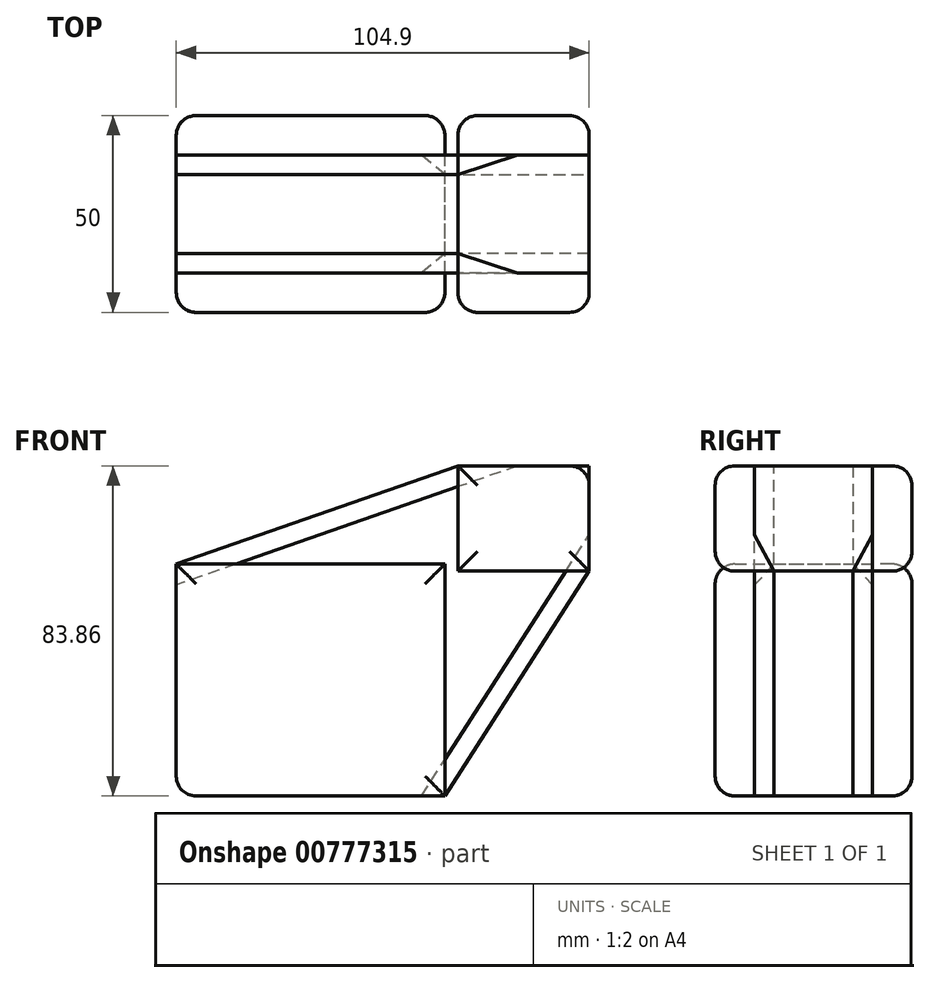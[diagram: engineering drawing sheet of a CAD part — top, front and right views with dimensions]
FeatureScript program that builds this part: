
annotation { "Feature Type Name" : "Feature", "Feature Type Description" : "" }
export const myFeature = defineFeature(function(context is Context, id is Id, definition is map)
    precondition{}
    {
        {
            var Q0;
            Q0=qCreatedBy(makeId("Front.planeOp"),FACE);
            var sketch = newSketch(context, id + "F0", { "sketchPlane" : qUnion([Q0])});
            skLineSegment(sketch, "E0.bottom", {"start": v(-34.72, 27.2) * mm, "end": v(33.51, 27.2) * mm});
            skLineSegment(sketch, "E0.top", {"start": v(-34.72, -31.71) * mm, "end": v(33.51, -31.71) * mm});
            skLineSegment(sketch, "E0.left", {"start": v(-34.72, 27.2) * mm, "end": v(-34.72, -31.71) * mm});
            skLineSegment(sketch, "E0.right", {"start": v(33.51, 27.2) * mm, "end": v(33.51, -31.71) * mm});
            skLineSegment(sketch, "E1.bottom", {"start": v(36.82, 52.15) * mm, "end": v(70.18, 52.15) * mm});
            skLineSegment(sketch, "E1.top", {"start": v(36.82, 25.4) * mm, "end": v(70.18, 25.4) * mm});
            skLineSegment(sketch, "E1.left", {"start": v(36.82, 52.15) * mm, "end": v(36.82, 25.4) * mm});
            skLineSegment(sketch, "E1.right", {"start": v(70.18, 52.15) * mm, "end": v(70.18, 25.4) * mm});
            skLineSegment(sketch, "E2", {"start": v(-34.72, 27.2) * mm, "end": v(36.82, 52.15) * mm});
            skLineSegment(sketch, "E3", {"start": v(33.51, -31.71) * mm, "end": v(70.18, 25.4) * mm});
            skSolve(sketch);
        }
        {
            var Q0;
            Q0=makeQuery(id+"F0.imprint","IMPRINT",FACE,{"disambiguationData":[TD([[makeQuery(id+"F0.imprint","IMPRINT",EDGE,{"derivedFrom":sQuery(id+"F0.wireOp",EDGE,"E0.bottom")}),-1.0]])]});
            var Q1;
            Q1=makeQuery(id+"F0.imprint","IMPRINT",FACE,{"disambiguationData":[TD([[makeQuery(id+"F0.imprint","IMPRINT",EDGE,{"derivedFrom":sQuery(id+"F0.wireOp",EDGE,"E1.bottom")}),-1.0]])]});
            extrude(context, id + "F1", {"entities" : qUnion([Q0, Q1]), "depth" : 40 * mm, "offsetDistance" : 25 * mm});
        }
        {
            var Q0;
            Q0 = qSketchRegion(id + "F0", true);
            extrude(context, id + "F2", {"entities" : qUnion([Q0]), "depth" : 30 * mm, "offsetDistance" : 25 * mm});
        }
        {
            var Q0;
            Q0=makeQuery(id+"F1.opExtrude","CAP_EDGE",EDGE,{"disambiguationData":[OSD([sQuery(id+"F0.wireOp",EDGE,"E0.bottom")])],"isStart":false});
            var Q1;
            Q1=makeQuery(id+"F1.opExtrude","CAP_EDGE",EDGE,{"disambiguationData":[OSD([sQuery(id+"F0.wireOp",EDGE,"E0.left")])],"isStart":false});
            var Q2;
            Q2=makeQuery(id+"F1.opExtrude","CAP_EDGE",EDGE,{"disambiguationData":[OSD([sQuery(id+"F0.wireOp",EDGE,"E0.top")])],"isStart":false});
            var Q3;
            Q3=makeQuery(id+"F1.opExtrude","CAP_EDGE",EDGE,{"disambiguationData":[OSD([sQuery(id+"F0.wireOp",EDGE,"E0.right")])],"isStart":false});
            fillet(context, id + "F3", {"entities" : qUnion([Q0, Q1, Q2, Q3]), "radius" : 5 * mm, "tangentPropagation" : true, "allowEdgeOverflow" : false});
        }
        {
            var Q0;
            Q0=makeQuery(id+"F2.opExtrude","CAP_EDGE",EDGE,{"disambiguationData":[OSD([sQuery(id+"F0.wireOp",EDGE,"E2")])],"isStart":false});
            var Q1;
            Q1=makeQuery(id+"F2.opExtrude","CAP_EDGE",EDGE,{"disambiguationData":[OSD([sQuery(id+"F0.wireOp",EDGE,"E2")])],"isStart":true});
            var Q2;
            Q2=makeQuery(id+"F2.opExtrude","CAP_EDGE",EDGE,{"disambiguationData":[OSD([sQuery(id+"F0.wireOp",EDGE,"E3")])],"isStart":false});
            var Q3;
            Q3=makeQuery(id+"F2.opExtrude","CAP_EDGE",EDGE,{"disambiguationData":[OSD([sQuery(id+"F0.wireOp",EDGE,"E3")])],"isStart":true});
            chamfer(context, id + "F4", {"entities" : qUnion([Q0, Q1, Q2, Q3]), "width" : 5 * mm, "tangentPropagation" : true});
        }
        {
            var Q0;
            Q0=makeQuery(id+"F1.opExtrude","CAP_FACE",FACE,{"disambiguationData":[OSD([sQuery(id+"F0.wireOp",EDGE,"E0.bottom"),sQuery(id+"F0.wireOp",EDGE,"E0.top"),sQuery(id+"F0.wireOp",EDGE,"E0.left"),sQuery(id+"F0.wireOp",EDGE,"E0.right")])],"isStart":true});
            var Q1;
            Q1=makeQuery(id+"F1.opExtrude","CAP_FACE",FACE,{"disambiguationData":[OSD([sQuery(id+"F0.wireOp",EDGE,"E1.bottom"),sQuery(id+"F0.wireOp",EDGE,"E1.top"),sQuery(id+"F0.wireOp",EDGE,"E1.left"),sQuery(id+"F0.wireOp",EDGE,"E1.right")])],"isStart":true});
            extrude(context, id + "F5", {"entities" : qUnion([Q0, Q1]), "depth" : 10 * mm, "offsetDistance" : 25 * mm});
        }
        {
            var Q0;
            Q0=makeQuery(id+"F1.opExtrude","CAP_EDGE",EDGE,{"disambiguationData":[OSD([sQuery(id+"F0.wireOp",EDGE,"E1.left")])],"isStart":false});
            var Q1;
            Q1=makeQuery(id+"F1.opExtrude","CAP_EDGE",EDGE,{"disambiguationData":[OSD([sQuery(id+"F0.wireOp",EDGE,"E1.right")])],"isStart":false});
            var Q2;
            Q2=makeQuery(id+"F1.opExtrude","CAP_EDGE",EDGE,{"disambiguationData":[OSD([sQuery(id+"F0.wireOp",EDGE,"E1.top")])],"isStart":false});
            var Q3;
            Q3=makeQuery(id+"F1.opExtrude","CAP_EDGE",EDGE,{"disambiguationData":[OSD([sQuery(id+"F0.wireOp",EDGE,"E1.bottom")])],"isStart":false});
            var Q4;
            Q4=makeQuery(id+"F5.opExtrude","CAP_EDGE",EDGE,{"disambiguationData":[OSD([sQuery(id+"F0.wireOp",EDGE,"E1.bottom")])],"isStart":false});
            var Q5;
            Q5=makeQuery(id+"F5.opExtrude","CAP_EDGE",EDGE,{"disambiguationData":[OSD([sQuery(id+"F0.wireOp",EDGE,"E1.right")])],"isStart":false});
            var Q6;
            Q6=makeQuery(id+"F5.opExtrude","CAP_EDGE",EDGE,{"disambiguationData":[OSD([sQuery(id+"F0.wireOp",EDGE,"E1.top")])],"isStart":false});
            var Q7;
            Q7=makeQuery(id+"F5.opExtrude","CAP_EDGE",EDGE,{"disambiguationData":[OSD([sQuery(id+"F0.wireOp",EDGE,"E1.left")])],"isStart":false});
            var Q8;
            Q8=makeQuery(id+"F5.opExtrude","CAP_EDGE",EDGE,{"disambiguationData":[OSD([sQuery(id+"F0.wireOp",EDGE,"E0.bottom")])],"isStart":false});
            var Q9;
            Q9=makeQuery(id+"F5.opExtrude","CAP_EDGE",EDGE,{"disambiguationData":[OSD([sQuery(id+"F0.wireOp",EDGE,"E0.right")])],"isStart":false});
            var Q10;
            Q10=makeQuery(id+"F5.opExtrude","CAP_EDGE",EDGE,{"disambiguationData":[OSD([sQuery(id+"F0.wireOp",EDGE,"E0.left")])],"isStart":false});
            var Q11;
            Q11=makeQuery(id+"F5.opExtrude","CAP_EDGE",EDGE,{"disambiguationData":[OSD([sQuery(id+"F0.wireOp",EDGE,"E0.top")])],"isStart":false});
            var Q12;
            Q12=makeQuery(id+"F1.opExtrude","SWEPT_EDGE",EDGE,{"disambiguationData":[OSD([sQuery(id+"F0.wireOp",EDGE,"E1.bottom"),sQuery(id+"F0.wireOp",EDGE,"E1.right")])]});
            var Q13;
            Q13=makeQuery(id+"F5.opExtrude","SWEPT_EDGE",EDGE,{"disambiguationData":[OSD([sQuery(id+"F0.wireOp",EDGE,"E1.bottom"),sQuery(id+"F0.wireOp",EDGE,"E1.right")])]});
            var Q14;
            Q14=makeQuery(id+"F2.opExtrude","SWEPT_EDGE",EDGE,{"disambiguationData":[OSD([sQuery(id+"F0.wireOp",EDGE,"E0.top"),sQuery(id+"F0.wireOp",EDGE,"E0.left")])]});
            var Q15;
            Q15=makeQuery(id+"F1.opExtrude","SWEPT_EDGE",EDGE,{"disambiguationData":[OSD([sQuery(id+"F0.wireOp",EDGE,"E0.top"),sQuery(id+"F0.wireOp",EDGE,"E0.left")])]});
            var Q16;
            Q16=makeQuery(id+"F5.opExtrude","SWEPT_EDGE",EDGE,{"disambiguationData":[OSD([sQuery(id+"F0.wireOp",EDGE,"E0.top"),sQuery(id+"F0.wireOp",EDGE,"E0.left")])]});
            fillet(context, id + "F6", {"entities" : qUnion([Q0, Q1, Q2, Q3, Q4, Q5, Q6, Q7, Q8, Q9, Q10, Q11, Q12, Q13, Q14, Q15, Q16]), "radius" : 5 * mm, "tangentPropagation" : true, "allowEdgeOverflow" : false});
        }
    });
